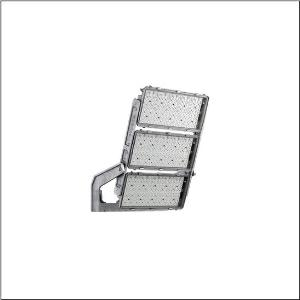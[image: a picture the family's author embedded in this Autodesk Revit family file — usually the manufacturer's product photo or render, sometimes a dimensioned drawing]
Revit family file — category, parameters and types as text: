
# Revit family: floodlight_fl_11_maxi_pro_remote___pl64blc_5xa779424w01aa_0c8b
name_source: partatom
category: Lighting Fixtures
units: mm (PartAtom-declared; Revit-internal decimal feet)

## family parameters
Cut with Voids When Loaded = No
Host = Face
Light Source = No
Part Type = Normal
Room Calculation Point = No
Round Connector Dimension = Use Diameter
Shared = No

## types (1)
- --- (1 x LED, 110040 lm, 1516.7 W, 5700K)
    Apparent Load = 1517 VA
    CIE Flux Codes = 28 83 99 100 100
    Color Rendering = 90
    Color Temperature = 5700K
    Default Elevation = 1800 mm
    Description = Floodlight FL 11  maxi  pro Remote floodlight; light control with lens of PMMA; cover panel of toughened safety glass, transparent; light distribution: PL64BLC, asymmetric direct distribution, LEDcolour temperature: 5700K, rated luminous flux: 110.040lm, colour rendering: CRI > 90, light colour: 957; luminous efficacy: 73lm/W; brightness control: DALI 2 (1 DALI address); with terminal, 8-pole, max. 2.5mm², mains connection: 220..240V/380..400V AC, 50/60Hz, surge voltage resistance: line to ground: 10kV, ECG replaceable separately, no afterglow with DALI off / DMX off command, LED unit replaceable without ESD environment, dustproof LED module, dimming range 10..100%; 1517W floodlight with 3x LED unit of diecast aluminium, coated grey; length: 1.003mm / width: 651mm / height: 338mm; mounting bracket, of diecast aluminium, uncoated, natural, equipment: Power, protection rating (complete): IP66; insulation class (complete): insulation class I (protective earthing); certification: CE; ball protection: ball impact resistance with accessories, impact resistance: IK07; only for outdoor installations, rated ambient temperature 10°C, permissible operating ambient temperature: -40..+30°C, permissible storage temperature: -40..+85°C; packaging unit: 1 piece

Light Distribution: PL64BLC
    Height = 320 mm
    Lamp = 1 x LED
    Lamp Light Flux = 110040 lm
    Lamp Power = 1516.7 W
    Lamp count = 1
    Length = 1002 mm
    Luminous efficacy = 73 lm/W
    Manufacturer = Siteco
    ModVariant = No
    Model = 5XA779424W01AA
    Mounting Place = Ceiling
    Mounting Type = Surface mounted
    Number of Poles = 1
    OnlyDefault = Yes
    Power Factor = 1
    Product Name = Floodlight FL 11 maxi pro Remote | PL64BLC
    Product group = floodlight | ceiling mounted
    ProductGroupID = 303
    Protection Class = Protection class I
    Protection Degree = IP 66
    RLX_Detail_Level = 1
    RLX_Emergency_Light_Flux = 0 lm
    RLX_Emergency_Type = 0
    RLX_Emergency_Type_DB = No
    RlxData = <blob elided: 52325 chars, md5=9386d864>
    Socket = socket
    Standby Power = 0 W
    System Light Flux = 110040 lm
    System Power = 1517 W
    Type Comments = factory setting: luminous flux: 100 % | dim-lin: 254 | 1070 mA
    Type Image = l_1006784.jpg
    URL = http://relux.com
    VarID = @adj_032541
    Voltage = 0 V
    Weight = 0.00 kg
    Width = 655 mm

## geometry (parser evidence)
native form markers: Blend x4, Sweep x14
no freeform markers — native parametric forms only
